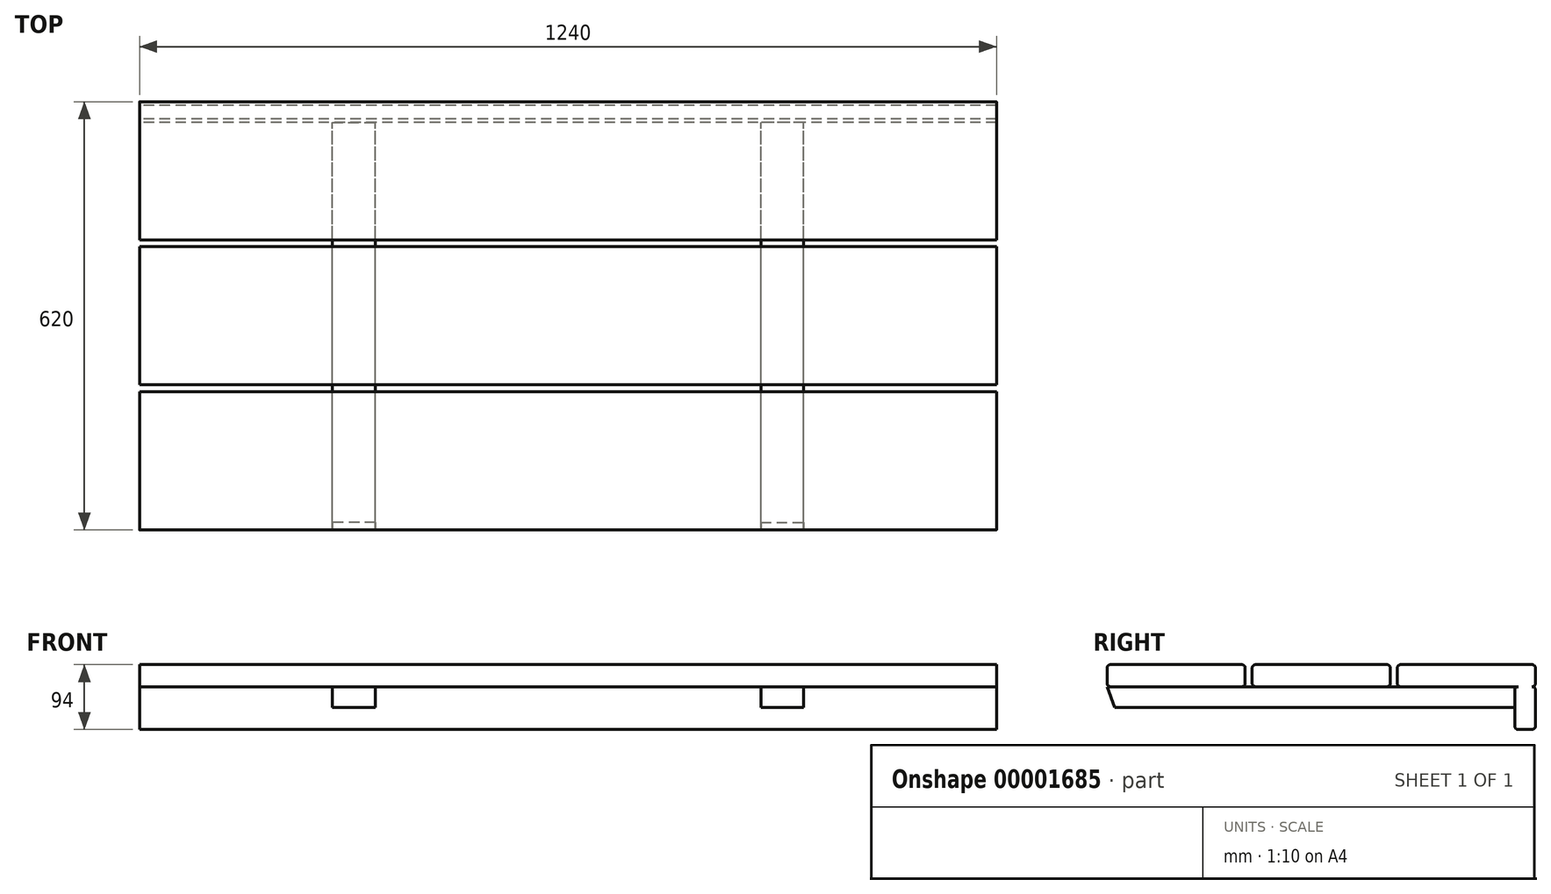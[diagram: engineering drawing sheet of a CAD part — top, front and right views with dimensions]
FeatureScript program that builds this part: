
annotation { "Feature Type Name" : "Feature", "Feature Type Description" : "" }
export const myFeature = defineFeature(function(context is Context, id is Id, definition is map)
    precondition{}
    {
        {
            var Q0;
            Q0=qCreatedBy(makeId("Right.planeOp"),FACE);
            var sketch = newSketch(context, id + "F0", { "sketchPlane" : qUnion([Q0])});
            skLineSegment(sketch, "E0.bottom", {"start": v(5, 0) * mm, "end": v(195, 0) * mm});
            skLineSegment(sketch, "E0.top", {"start": v(5, 32) * mm, "end": v(195, 32) * mm});
            skLineSegment(sketch, "E0.left", {"start": v(0, 5) * mm, "end": v(0, 27) * mm});
            skLineSegment(sketch, "E0.right", {"start": v(200, 5) * mm, "end": v(200, 27) * mm});
            skPoint(sketch, "E1.visualSharp", {"position": v(0, 32) * mm});
            skArc(sketch, "E1.filletArc", {"start": v(5, 32) * mm, "mid": v(1.46, 30.54) * mm, "end": v(0, 27) * mm});
            skPoint(sketch, "E2.visualSharp", {"position": v(0, 0) * mm});
            skArc(sketch, "E2.filletArc", {"start": v(0, 5) * mm, "mid": v(1.46, 1.46) * mm, "end": v(5, 0) * mm});
            skPoint(sketch, "E3.visualSharp", {"position": v(200, 0) * mm});
            skArc(sketch, "E3.filletArc", {"start": v(195, 0) * mm, "mid": v(198.54, 1.46) * mm, "end": v(200, 5) * mm});
            skPoint(sketch, "E4.visualSharp", {"position": v(200, 32) * mm});
            skArc(sketch, "E4.filletArc", {"start": v(200, 27) * mm, "mid": v(198.54, 30.54) * mm, "end": v(195, 32) * mm});
            skLineSegment(sketch, "E5.bottom", {"start": v(215, 0) * mm, "end": v(405, 0) * mm});
            skLineSegment(sketch, "E5.top", {"start": v(215, 32) * mm, "end": v(405, 32) * mm});
            skLineSegment(sketch, "E5.left", {"start": v(210, 5) * mm, "end": v(210, 27) * mm});
            skLineSegment(sketch, "E5.right", {"start": v(410, 5) * mm, "end": v(410, 27) * mm});
            skPoint(sketch, "E6.visualSharp", {"position": v(410, 32) * mm});
            skArc(sketch, "E6.filletArc", {"start": v(410, 27) * mm, "mid": v(408.54, 30.54) * mm, "end": v(405, 32) * mm});
            skPoint(sketch, "E7.visualSharp", {"position": v(210, 32) * mm});
            skArc(sketch, "E7.filletArc", {"start": v(215, 32) * mm, "mid": v(211.46, 30.54) * mm, "end": v(210, 27) * mm});
            skPoint(sketch, "E8.visualSharp", {"position": v(210, 0) * mm});
            skArc(sketch, "E8.filletArc", {"start": v(210, 5) * mm, "mid": v(211.46, 1.46) * mm, "end": v(215, 0) * mm});
            skPoint(sketch, "E9.visualSharp", {"position": v(410, 0) * mm});
            skArc(sketch, "E9.filletArc", {"start": v(405, 0) * mm, "mid": v(408.54, 1.46) * mm, "end": v(410, 5) * mm});
            skLineSegment(sketch, "E10.bottom", {"start": v(425, 32) * mm, "end": v(615, 32) * mm});
            skLineSegment(sketch, "E10.top", {"start": v(425, 0) * mm, "end": v(615, 0) * mm});
            skLineSegment(sketch, "E10.left", {"start": v(420, 27) * mm, "end": v(420, 5) * mm});
            skLineSegment(sketch, "E10.right", {"start": v(620, 27) * mm, "end": v(620, 5) * mm});
            skPoint(sketch, "E11.visualSharp", {"position": v(420, 32) * mm});
            skArc(sketch, "E11.filletArc", {"start": v(425, 32) * mm, "mid": v(421.46, 30.54) * mm, "end": v(420, 27) * mm});
            skPoint(sketch, "E12.visualSharp", {"position": v(420, 0) * mm});
            skArc(sketch, "E12.filletArc", {"start": v(420, 5) * mm, "mid": v(421.46, 1.46) * mm, "end": v(425, 0) * mm});
            skPoint(sketch, "E13.visualSharp", {"position": v(620, 32) * mm});
            skArc(sketch, "E13.filletArc", {"start": v(620, 27) * mm, "mid": v(618.54, 30.54) * mm, "end": v(615, 32) * mm});
            skPoint(sketch, "E14.visualSharp", {"position": v(620, 0) * mm});
            skArc(sketch, "E14.filletArc", {"start": v(615, 0) * mm, "mid": v(618.54, 1.46) * mm, "end": v(620, 5) * mm});
            skSolve(sketch);
        }
        {
            var Q0;
            Q0=makeQuery(id+"F0.imprint","IMPRINT",FACE,{"disambiguationData":[TD([[makeQuery(id+"F0.imprint","IMPRINT",EDGE,{"derivedFrom":sQuery(id+"F0.wireOp",EDGE,"E0.bottom")}),1.0]])]});
            var Q1;
            Q1=makeQuery(id+"F0.imprint","IMPRINT",FACE,{"disambiguationData":[TD([[makeQuery(id+"F0.imprint","IMPRINT",EDGE,{"derivedFrom":sQuery(id+"F0.wireOp",EDGE,"E5.bottom")}),1.0]])]});
            var Q2;
            Q2=makeQuery(id+"F0.imprint","IMPRINT",FACE,{"disambiguationData":[TD([[makeQuery(id+"F0.imprint","IMPRINT",EDGE,{"derivedFrom":sQuery(id+"F0.wireOp",EDGE,"E10.bottom")}),-1.0]])]});
            extrude(context, id + "F1", {"entities" : qUnion([Q0, Q1, Q2]), "depth" : 1240 * mm});
        }
        {
            var Q0;
            Q0=makeQuery(id+"F1.opExtrude","CAP_FACE",FACE,{"disambiguationData":[OSD([sQuery(id+"F0.wireOp",EDGE,"E10.bottom"),sQuery(id+"F0.wireOp",EDGE,"E10.top"),sQuery(id+"F0.wireOp",EDGE,"E10.left"),sQuery(id+"F0.wireOp",EDGE,"E10.right"),sQuery(id+"F0.wireOp",EDGE,"E11.filletArc"),sQuery(id+"F0.wireOp",EDGE,"E12.filletArc"),sQuery(id+"F0.wireOp",EDGE,"E13.filletArc"),sQuery(id+"F0.wireOp",EDGE,"E14.filletArc")])],"isStart":true});
            var sketch = newSketch(context, id + "F2", { "sketchPlane" : qUnion([Q0])});
            skLineSegment(sketch, "E15.bottom", {"start": v(-615, -62) * mm, "end": v(-595, -62) * mm});
            skLineSegment(sketch, "E15.top", {"start": v(-615, 0) * mm, "end": v(-595, 0) * mm});
            skLineSegment(sketch, "E15.left", {"start": v(-620, -57) * mm, "end": v(-620, -5) * mm});
            skLineSegment(sketch, "E15.right", {"start": v(-590, -57) * mm, "end": v(-590, -5) * mm});
            skPoint(sketch, "E16.visualSharp", {"position": v(-620, 0) * mm});
            skArc(sketch, "E16.filletArc", {"start": v(-615, 0) * mm, "mid": v(-618.54, -1.46) * mm, "end": v(-620, -5) * mm});
            skPoint(sketch, "E17.visualSharp", {"position": v(-590, 0) * mm});
            skArc(sketch, "E17.filletArc", {"start": v(-590, -5) * mm, "mid": v(-591.46, -1.46) * mm, "end": v(-595, 0) * mm});
            skPoint(sketch, "E18.visualSharp", {"position": v(-590, -62) * mm});
            skArc(sketch, "E18.filletArc", {"start": v(-595, -62) * mm, "mid": v(-591.46, -60.54) * mm, "end": v(-590, -57) * mm});
            skPoint(sketch, "E19.visualSharp", {"position": v(-620, -62) * mm});
            skArc(sketch, "E19.filletArc", {"start": v(-620, -57) * mm, "mid": v(-618.54, -60.54) * mm, "end": v(-615, -62) * mm});
            skSolve(sketch);
        }
        {
            var Q0;
            Q0=makeQuery(id+"F2.imprint","IMPRINT",FACE,{"disambiguationData":[TD([[makeQuery(id+"F2.imprint","IMPRINT",EDGE,{"derivedFrom":sQuery(id+"F2.wireOp",EDGE,"E15.bottom")}),1.0]])]});
            var Q1;
            Q1=makeQuery(id+"F1.opExtrude","CAP_FACE",FACE,{"disambiguationData":[OSD([sQuery(id+"F0.wireOp",EDGE,"E10.bottom"),sQuery(id+"F0.wireOp",EDGE,"E10.top"),sQuery(id+"F0.wireOp",EDGE,"E10.left"),sQuery(id+"F0.wireOp",EDGE,"E10.right"),sQuery(id+"F0.wireOp",EDGE,"E11.filletArc"),sQuery(id+"F0.wireOp",EDGE,"E12.filletArc"),sQuery(id+"F0.wireOp",EDGE,"E13.filletArc"),sQuery(id+"F0.wireOp",EDGE,"E14.filletArc")])],"isStart":false});
            extrude(context, id + "F3", {"entities" : qUnion([Q0]), "operationType" : NewBodyOperationType.ADD, "endBound" : BoundingType.UP_TO_SURFACE, "oppositeDirection" : true, "endBoundEntityFace" : qUnion([Q1]), "depth" : 25 * mm});
        }
        {
            var Q0;
            Q0=makeQuery(id+"F1.opExtrude","CAP_FACE",FACE,{"disambiguationData":[OSD([sQuery(id+"F0.wireOp",EDGE,"E5.bottom"),sQuery(id+"F0.wireOp",EDGE,"E5.top"),sQuery(id+"F0.wireOp",EDGE,"E5.left"),sQuery(id+"F0.wireOp",EDGE,"E5.right"),sQuery(id+"F0.wireOp",EDGE,"E6.filletArc"),sQuery(id+"F0.wireOp",EDGE,"E7.filletArc"),sQuery(id+"F0.wireOp",EDGE,"E8.filletArc"),sQuery(id+"F0.wireOp",EDGE,"E9.filletArc")])],"isStart":true});
            cPlane(context, id + "F4", {"entities" : qUnion([Q0]), "cplaneType" : CPlaneType.OFFSET, "offset" : 620 * mm, "oppositeDirection" : true, "width" : 150 * mm, "height" : 150 * mm});
        }
        {
            var Q0;
            Q0=makeQuery(id+"F3.opExtrude","SWEPT_FACE",FACE,{"disambiguationData":[OSD([sQuery(id+"F2.wireOp",EDGE,"E15.right")])]});
            var sketch = newSketch(context, id + "F5", { "sketchPlane" : qUnion([Q0])});
            skLineSegment(sketch, "E20.bottom", {"start": v(279, -30) * mm, "end": v(341, -30) * mm});
            skLineSegment(sketch, "E20.top", {"start": v(279, 0) * mm, "end": v(341, 0) * mm});
            skLineSegment(sketch, "E20.left", {"start": v(279, -30) * mm, "end": v(279, 0) * mm});
            skLineSegment(sketch, "E20.right", {"start": v(341, -30) * mm, "end": v(341, 0) * mm});
            skLineSegment(sketch, "E21", {"start": v(310, -30) * mm, "end": v(310, 0) * mm});
            skSolve(sketch);
        }
        {
            var Q0;
            {var subQ3=sQuery(id+"F5.wireOp",EDGE,"E20.left");var subQ6=sQuery(id+"F5.wireOp",EDGE,"E20.top");var subQ9=makeQuery(id+"F5.imprint","INTERSECT",VERTEX,{"derivedFrom":[subQ6,subQ3]});var subQ10=sQuery(id+"F5.wireOp",EDGE,"E20.right");var subQ13=makeQuery(id+"F5.imprint","INTERSECT",VERTEX,{"derivedFrom":[subQ6,subQ10]});var subQ14=sQuery(id+"F5.wireOp",EDGE,"E20.bottom");var subQ17=makeQuery(id+"F5.imprint","INTERSECT",VERTEX,{"derivedFrom":[subQ14,subQ3]});var subQ18=makeQuery(id+"F5.imprint","INTERSECT",VERTEX,{"derivedFrom":[subQ14,subQ10]});Q0=qUnion([makeQuery(id+"F5.imprint","IMPRINT",FACE,{"disambiguationData":[TD([[makeQuery(id+"F5.imprint","IMPRINT",EDGE,{"disambiguationData":[TD([[subQ9,-1.0]])],"derivedFrom":subQ6}),-1.0]])]}),makeQuery(id+"F5.imprint","IMPRINT",FACE,{"disambiguationData":[TD([[makeQuery(id+"F5.imprint","IMPRINT",EDGE,{"disambiguationData":[TD([[subQ13,1.0]])],"derivedFrom":subQ6}),-1.0]])]}),makeQuery(id+"F5.imprint","IMPRINT",FACE,{"disambiguationData":[TD([[makeQuery(id+"F5.imprint","IMPRINT",EDGE,{"disambiguationData":[TD([[subQ17,-1.0]])],"derivedFrom":subQ14}),1.0]])]}),makeQuery(id+"F5.imprint","IMPRINT",FACE,{"disambiguationData":[TD([[makeQuery(id+"F5.imprint","IMPRINT",EDGE,{"disambiguationData":[TD([[subQ18,1.0]])],"derivedFrom":subQ14}),1.0]])]})]);}
            extrude(context, id + "F6", {"entities" : qUnion([Q0]), "depth" : 662.48 * mm});
        }
        {
            var Q0;
            Q0=makeQuery(id+"F6.opExtrude","SWEPT_FACE",FACE,{"disambiguationData":[OSD([sQuery(id+"F5.wireOp",EDGE,"E20.left")])]});
            var sketch = newSketch(context, id + "F7", { "sketchPlane" : qUnion([Q0])});
            skLineSegment(sketch, "E22", {"start": v(-10.92, -30) * mm, "end": v(0, 0) * mm});
            skSolve(sketch);
        }
        {
            var Q0;
            Q0 = qSketchRegion(id + "F7", true);
            var Q1;
            {var subQ2=sQuery(id+"F7.wireOp",EDGE,"E22");Q1=makeQuery(id+"F7.imprint","IMPRINT",FACE,{"disambiguationData":[TD([[makeQuery(id+"F7.imprint","IMPRINT",EDGE,{"derivedFrom":subQ2}),-1.0]])]});}
            extrude(context, id + "F8", {"entities" : qUnion([Q0, Q1]), "operationType" : NewBodyOperationType.REMOVE, "endBound" : BoundingType.THROUGH_ALL, "oppositeDirection" : true, "depth" : 25 * mm});
        }
        {
            var Q0;
            Q0=makeQuery(id+"F6.opExtrude","SWEPT_BODY",BODY,{"disambiguationData":[OSD([sQuery(id+"F5.wireOp",EDGE,"E20.bottom"),sQuery(id+"F5.wireOp",EDGE,"E20.top"),sQuery(id+"F5.wireOp",EDGE,"E20.left"),sQuery(id+"F5.wireOp",EDGE,"E20.right")])]});
            var Q1;
            Q1=qCreatedBy(id+"F4.planeOp",FACE);
            mirror(context, id + "F9", {"entities" : qUnion([Q0]), "mirrorPlane" : qUnion([Q1])});
        }
    });
